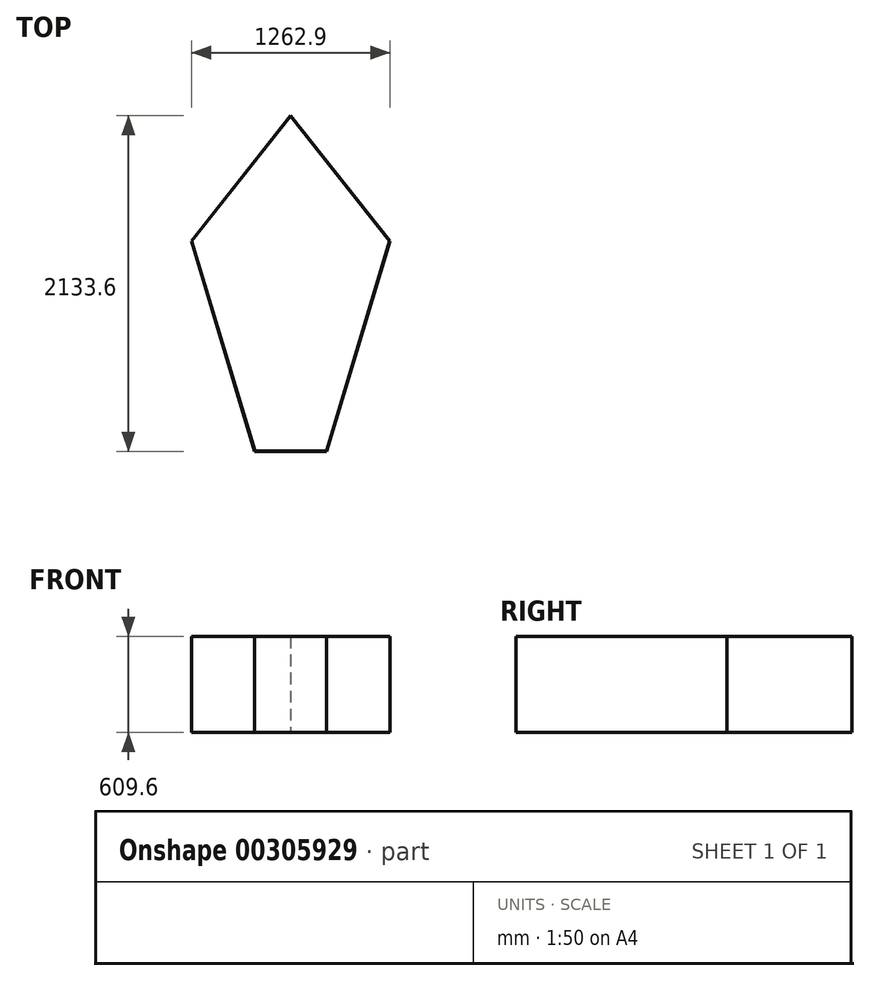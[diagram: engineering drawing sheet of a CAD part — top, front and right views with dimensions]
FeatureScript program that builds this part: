
annotation { "Feature Type Name" : "Feature", "Feature Type Description" : "" }
export const myFeature = defineFeature(function(context is Context, id is Id, definition is map)
    precondition{}
    {
        {
            var Q0;
            Q0=qCreatedBy(makeId("Top.planeOp"),FACE);
            var sketch = newSketch(context, id + "F0", { "sketchPlane" : qUnion([Q0])});
            skLineSegment(sketch, "E0", {"start": v(0, 0) * mm, "end": v(0, 2133.6) * mm});
            skLineSegment(sketch, "E1", {"start": v(0, 0) * mm, "end": v(-228.6, 0) * mm});
            skLineSegment(sketch, "E2.MirrorCS", {"start": v(0, 0) * mm, "end": v(228.6, 0) * mm});
            skLineSegment(sketch, "E3", {"start": v(-228.6, 0) * mm, "end": v(-631.45, 1337.66) * mm});
            skLineSegment(sketch, "E4", {"start": v(-631.45, 1337.66) * mm, "end": v(0, 2133.6) * mm});
            skLineSegment(sketch, "E5", {"start": v(228.6, 0) * mm, "end": v(631.45, 1337.66) * mm});
            skLineSegment(sketch, "E6", {"start": v(631.45, 1337.66) * mm, "end": v(0, 2133.6) * mm});
            skSolve(sketch);
        }
        {
            var Q0;
            Q0 = qSketchRegion(id + "F0", true);
            extrude(context, id + "F1", {"entities" : qUnion([Q0]), "depth" : 609.6 * mm});
        }
        {
            var Q0;
            Q0=makeQuery(id+"F1.opExtrude","CAP_FACE",FACE,{"disambiguationData":[OSD([sQuery(id+"F0.wireOp",EDGE,"E1"),sQuery(id+"F0.wireOp",EDGE,"E2.MirrorCS"),sQuery(id+"F0.wireOp",EDGE,"E3"),sQuery(id+"F0.wireOp",EDGE,"E4"),sQuery(id+"F0.wireOp",EDGE,"E5"),sQuery(id+"F0.wireOp",EDGE,"E6")])],"isStart":false});
            shell(context, id + "F2", {"entities" : qUnion([Q0]), "thickness" : 2.54 * mm});
        }
    });
